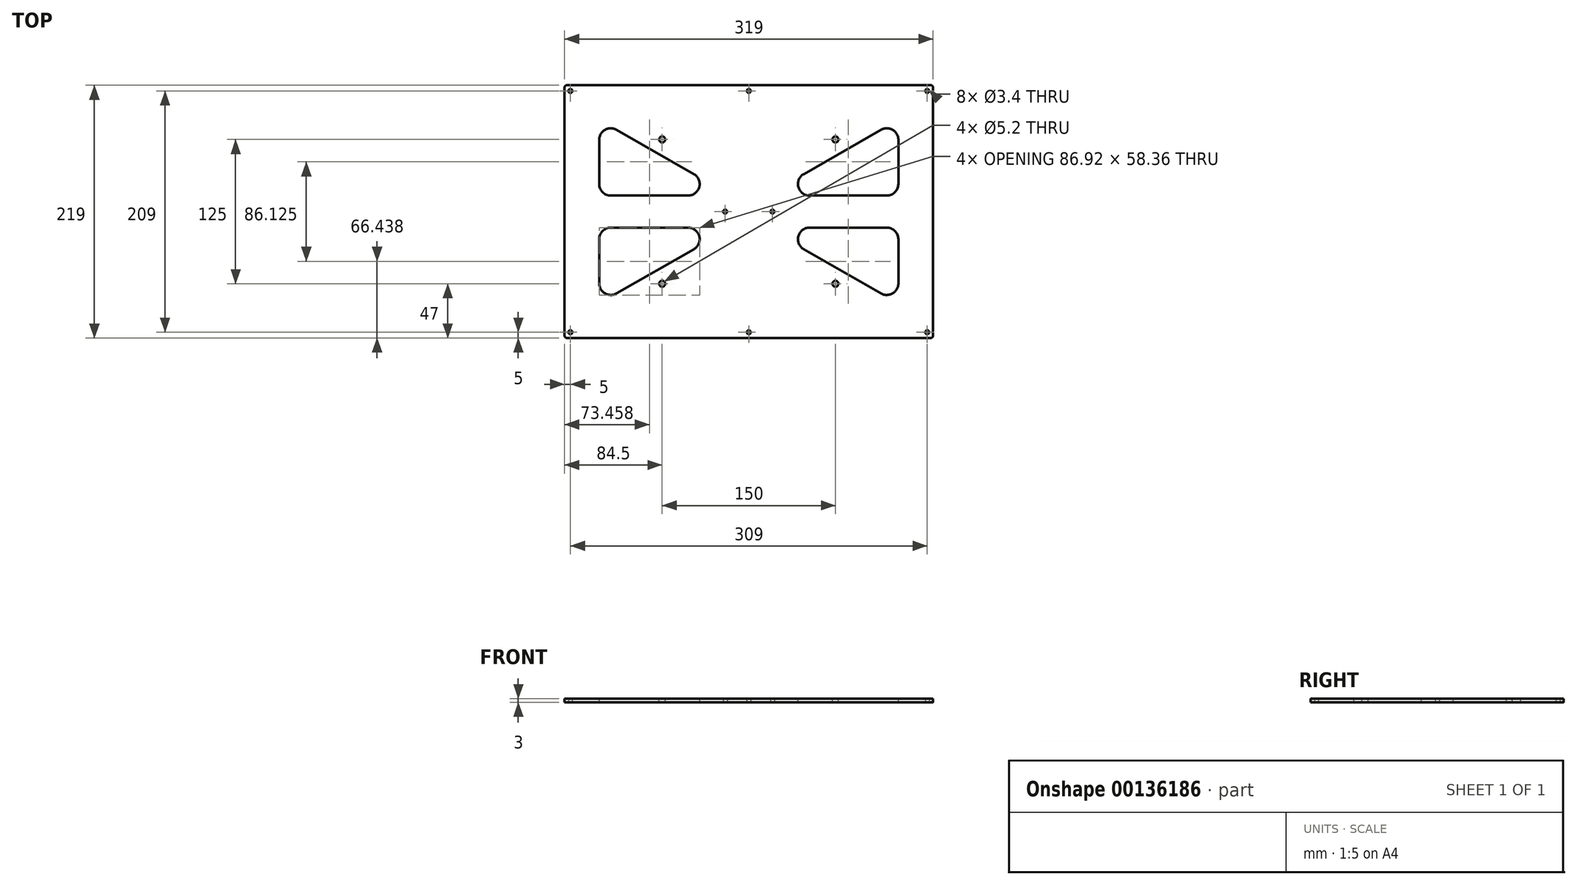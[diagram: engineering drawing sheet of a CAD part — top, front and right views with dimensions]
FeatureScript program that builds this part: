
annotation { "Feature Type Name" : "Feature", "Feature Type Description" : "" }
export const myFeature = defineFeature(function(context is Context, id is Id, definition is map)
    precondition{}
    {
        {
            var Q0;
            Q0=qCreatedBy(makeId("Top.planeOp"),FACE);
            var sketch = newSketch(context, id + "F0", { "sketchPlane" : qUnion([Q0])});
            skLineSegment(sketch, "E0.bottom", {"start": v(157.5, -109.5) * mm, "end": v(-157.5, -109.5) * mm});
            skLineSegment(sketch, "E0.top", {"start": v(157.5, 109.5) * mm, "end": v(-157.5, 109.5) * mm});
            skLineSegment(sketch, "E0.left", {"start": v(159.5, -107.5) * mm, "end": v(159.5, 107.5) * mm});
            skLineSegment(sketch, "E0.right", {"start": v(-159.5, -107.5) * mm, "end": v(-159.5, 107.5) * mm});
            skPoint(sketch, "E0.middle", {"position": v(0, 0) * mm});
            skPoint(sketch, "E1.visualSharp", {"position": v(-159.5, 109.5) * mm});
            skArc(sketch, "E1.filletArc", {"start": v(-157.5, 109.5) * mm, "mid": v(-158.91, 108.91) * mm, "end": v(-159.5, 107.5) * mm});
            skPoint(sketch, "E2.visualSharp", {"position": v(159.5, 109.5) * mm});
            skArc(sketch, "E2.filletArc", {"start": v(159.5, 107.5) * mm, "mid": v(158.91, 108.91) * mm, "end": v(157.5, 109.5) * mm});
            skPoint(sketch, "E3.visualSharp", {"position": v(159.5, -109.5) * mm});
            skArc(sketch, "E3.filletArc", {"start": v(157.5, -109.5) * mm, "mid": v(158.91, -108.91) * mm, "end": v(159.5, -107.5) * mm});
            skPoint(sketch, "E4.visualSharp", {"position": v(-159.5, -109.5) * mm});
            skArc(sketch, "E4.filletArc", {"start": v(-159.5, -107.5) * mm, "mid": v(-158.91, -108.91) * mm, "end": v(-157.5, -109.5) * mm});
            skLineSegment(sketch, "E5.bottom", {"start": v(154.5, -104.5) * mm, "end": v(-154.5, -104.5) * mm, "construction": true});
            skLineSegment(sketch, "E5.top", {"start": v(154.5, 104.5) * mm, "end": v(-154.5, 104.5) * mm, "construction": true});
            skLineSegment(sketch, "E5.left", {"start": v(154.5, -104.5) * mm, "end": v(154.5, 104.5) * mm, "construction": true});
            skLineSegment(sketch, "E5.right", {"start": v(-154.5, -104.5) * mm, "end": v(-154.5, 104.5) * mm, "construction": true});
            skLineSegment(sketch, "E6", {"start": v(0, 104.5) * mm, "end": v(0, -104.5) * mm, "construction": true});
            skCircle(sketch, "E7", {"center": v(-154.5, 104.5) * mm, "radius": 1.7 * mm});
            skCircle(sketch, "E8", {"center": v(0, 104.5) * mm, "radius": 1.7 * mm});
            skCircle(sketch, "E9", {"center": v(154.5, 104.5) * mm, "radius": 1.7 * mm});
            skCircle(sketch, "E10", {"center": v(154.5, -104.5) * mm, "radius": 1.7 * mm});
            skCircle(sketch, "E11", {"center": v(0, -104.5) * mm, "radius": 1.7 * mm});
            skCircle(sketch, "E12", {"center": v(-154.5, -104.5) * mm, "radius": 1.7 * mm});
            skLineSegment(sketch, "E13", {"start": v(-154.5, 0) * mm, "end": v(159.5, 0) * mm, "construction": true});
            skCircle(sketch, "E14", {"center": v(-20.5, 0) * mm, "radius": 1.7 * mm});
            skCircle(sketch, "E15", {"center": v(20.5, 0) * mm, "radius": 1.7 * mm});
            skSolve(sketch);
        }
        {
            var Q0;
            Q0 = qSketchRegion(id + "F0", true);
            extrude(context, id + "F1", {"entities" : qUnion([Q0]), "depth" : 3 * mm});
        }
        {
            var Q0;
            Q0=makeQuery(id+"F1.opExtrude","CAP_FACE",FACE,{"disambiguationData":[OSD([sQuery(id+"F0.wireOp",EDGE,"E0.bottom"),sQuery(id+"F0.wireOp",EDGE,"E0.top"),sQuery(id+"F0.wireOp",EDGE,"E0.left"),sQuery(id+"F0.wireOp",EDGE,"E0.right"),sQuery(id+"F0.wireOp",EDGE,"E1.filletArc"),sQuery(id+"F0.wireOp",EDGE,"E2.filletArc"),sQuery(id+"F0.wireOp",EDGE,"E3.filletArc"),sQuery(id+"F0.wireOp",EDGE,"E4.filletArc"),sQuery(id+"F0.wireOp",EDGE,"E7"),sQuery(id+"F0.wireOp",EDGE,"E8"),sQuery(id+"F0.wireOp",EDGE,"E9"),sQuery(id+"F0.wireOp",EDGE,"E10"),sQuery(id+"F0.wireOp",EDGE,"E11"),sQuery(id+"F0.wireOp",EDGE,"E12"),sQuery(id+"F0.wireOp",EDGE,"E14"),sQuery(id+"F0.wireOp",EDGE,"E15")])],"isStart":false});
            var sketch = newSketch(context, id + "F2", { "sketchPlane" : qUnion([Q0])});
            skLineSegment(sketch, "E16.left", {"start": v(129.5, -62.24) * mm, "end": v(129.5, -23.88) * mm});
            skLineSegment(sketch, "E16.right", {"start": v(-129.5, -62.24) * mm, "end": v(-129.5, -23.88) * mm});
            skPoint(sketch, "E16.middle", {"position": v(0, 0) * mm});
            skLineSegment(sketch, "E17.bottom", {"start": v(119.5, -13.88) * mm, "end": v(52.56, -13.88) * mm});
            skLineSegment(sketch, "E17.top", {"start": v(119.5, 13.88) * mm, "end": v(52.56, 13.88) * mm});
            skLineSegment(sketch, "E18.trimOffspring", {"start": v(129.5, 23.88) * mm, "end": v(129.5, 62.24) * mm});
            skLineSegment(sketch, "E19.trimOffspring", {"start": v(-129.5, 23.88) * mm, "end": v(-129.5, 62.24) * mm});
            skLineSegment(sketch, "E20.trimOffspring", {"start": v(-52.56, 13.88) * mm, "end": v(-119.5, 13.88) * mm});
            skLineSegment(sketch, "E21.trimOffspring", {"start": v(-52.56, -13.88) * mm, "end": v(-119.5, -13.88) * mm});
            skLineSegment(sketch, "E22", {"start": v(-47.59, -32.56) * mm, "end": v(-114.53, -70.92) * mm});
            skLineSegment(sketch, "E23", {"start": v(47.59, -32.56) * mm, "end": v(114.53, -70.92) * mm});
            skLineSegment(sketch, "E24", {"start": v(47.59, 32.56) * mm, "end": v(114.53, 70.92) * mm});
            skLineSegment(sketch, "E25", {"start": v(-47.59, 32.56) * mm, "end": v(-114.53, 70.92) * mm});
            skPoint(sketch, "E26.top.end.orphan", {"position": v(-15, 79.5) * mm});
            skPoint(sketch, "E16.top.end.orphan", {"position": v(15, 79.5) * mm});
            skPoint(sketch, "E27.visualSharp", {"position": v(-129.5, 13.88) * mm});
            skArc(sketch, "E27.filletArc", {"start": v(-129.5, 23.88) * mm, "mid": v(-126.57, 16.81) * mm, "end": v(-119.5, 13.88) * mm});
            skPoint(sketch, "E28.visualSharp", {"position": v(-129.5, 79.5) * mm});
            skArc(sketch, "E28.filletArc", {"start": v(-114.53, 70.92) * mm, "mid": v(-124.51, 70.9) * mm, "end": v(-129.5, 62.24) * mm});
            skPoint(sketch, "E29.visualSharp", {"position": v(-15, 13.88) * mm});
            skArc(sketch, "E29.filletArc", {"start": v(-52.56, 13.88) * mm, "mid": v(-42.9, 21.3) * mm, "end": v(-47.59, 32.56) * mm});
            skPoint(sketch, "E30.visualSharp", {"position": v(-15, -13.88) * mm});
            skArc(sketch, "E30.filletArc", {"start": v(-47.59, -32.56) * mm, "mid": v(-42.9, -21.3) * mm, "end": v(-52.56, -13.88) * mm});
            skPoint(sketch, "E31.visualSharp", {"position": v(-129.5, -13.88) * mm});
            skArc(sketch, "E31.filletArc", {"start": v(-119.5, -13.88) * mm, "mid": v(-126.57, -16.81) * mm, "end": v(-129.5, -23.88) * mm});
            skPoint(sketch, "E32.visualSharp", {"position": v(-129.5, -79.5) * mm});
            skArc(sketch, "E32.filletArc", {"start": v(-129.5, -62.24) * mm, "mid": v(-124.51, -70.9) * mm, "end": v(-114.53, -70.92) * mm});
            skPoint(sketch, "E33.visualSharp", {"position": v(15, -13.88) * mm});
            skArc(sketch, "E33.filletArc", {"start": v(52.56, -13.88) * mm, "mid": v(42.9, -21.3) * mm, "end": v(47.59, -32.56) * mm});
            skPoint(sketch, "E34.visualSharp", {"position": v(129.5, -13.88) * mm});
            skArc(sketch, "E34.filletArc", {"start": v(129.5, -23.88) * mm, "mid": v(126.57, -16.81) * mm, "end": v(119.5, -13.88) * mm});
            skPoint(sketch, "E35.visualSharp", {"position": v(129.5, -79.5) * mm});
            skArc(sketch, "E35.filletArc", {"start": v(114.53, -70.92) * mm, "mid": v(124.51, -70.9) * mm, "end": v(129.5, -62.24) * mm});
            skPoint(sketch, "E36.visualSharp", {"position": v(15, 13.88) * mm});
            skArc(sketch, "E36.filletArc", {"start": v(47.59, 32.56) * mm, "mid": v(42.9, 21.3) * mm, "end": v(52.56, 13.88) * mm});
            skPoint(sketch, "E37.visualSharp", {"position": v(129.5, 79.5) * mm});
            skArc(sketch, "E37.filletArc", {"start": v(129.5, 62.24) * mm, "mid": v(124.51, 70.9) * mm, "end": v(114.53, 70.92) * mm});
            skPoint(sketch, "E38.visualSharp", {"position": v(129.5, 13.88) * mm});
            skArc(sketch, "E38.filletArc", {"start": v(119.5, 13.88) * mm, "mid": v(126.57, 16.81) * mm, "end": v(129.5, 23.88) * mm});
            skSolve(sketch);
        }
        {
            var Q0;
            Q0=makeQuery(id+"F2.imprint","IMPRINT",FACE,{"disambiguationData":[TD([[makeQuery(id+"F2.imprint","IMPRINT",EDGE,{"derivedFrom":sQuery(id+"F2.wireOp",EDGE,"E19.trimOffspring")}),-1.0]])]});
            var Q1;
            Q1=makeQuery(id+"F2.imprint","IMPRINT",FACE,{"disambiguationData":[TD([[makeQuery(id+"F2.imprint","IMPRINT",EDGE,{"derivedFrom":sQuery(id+"F2.wireOp",EDGE,"E17.top")}),-1.0]])]});
            var Q2;
            Q2=makeQuery(id+"F2.imprint","IMPRINT",FACE,{"disambiguationData":[TD([[makeQuery(id+"F2.imprint","IMPRINT",EDGE,{"derivedFrom":sQuery(id+"F2.wireOp",EDGE,"E16.left")}),1.0]])]});
            var Q3;
            Q3=makeQuery(id+"F2.imprint","IMPRINT",FACE,{"disambiguationData":[TD([[makeQuery(id+"F2.imprint","IMPRINT",EDGE,{"derivedFrom":sQuery(id+"F2.wireOp",EDGE,"E16.right")}),-1.0]])]});
            extrude(context, id + "F3", {"entities" : qUnion([Q0, Q1, Q2, Q3]), "operationType" : NewBodyOperationType.REMOVE, "endBound" : BoundingType.THROUGH_ALL, "oppositeDirection" : true, "depth" : 25 * mm});
        }
        {
            var Q0;
            Q0=makeQuery(id+"F1.opExtrude","CAP_FACE",FACE,{"disambiguationData":[OSD([sQuery(id+"F0.wireOp",EDGE,"E0.bottom"),sQuery(id+"F0.wireOp",EDGE,"E0.top"),sQuery(id+"F0.wireOp",EDGE,"E0.left"),sQuery(id+"F0.wireOp",EDGE,"E0.right"),sQuery(id+"F0.wireOp",EDGE,"E1.filletArc"),sQuery(id+"F0.wireOp",EDGE,"E2.filletArc"),sQuery(id+"F0.wireOp",EDGE,"E3.filletArc"),sQuery(id+"F0.wireOp",EDGE,"E4.filletArc"),sQuery(id+"F0.wireOp",EDGE,"E7"),sQuery(id+"F0.wireOp",EDGE,"E8"),sQuery(id+"F0.wireOp",EDGE,"E9"),sQuery(id+"F0.wireOp",EDGE,"E10"),sQuery(id+"F0.wireOp",EDGE,"E11"),sQuery(id+"F0.wireOp",EDGE,"E12"),sQuery(id+"F0.wireOp",EDGE,"E14"),sQuery(id+"F0.wireOp",EDGE,"E15")])],"isStart":false});
            var sketch = newSketch(context, id + "F4", { "sketchPlane" : qUnion([Q0])});
            skLineSegment(sketch, "E39.bottom", {"start": v(75, -62.5) * mm, "end": v(-75, -62.5) * mm, "construction": true});
            skLineSegment(sketch, "E39.top", {"start": v(75, 62.5) * mm, "end": v(-75, 62.5) * mm, "construction": true});
            skLineSegment(sketch, "E39.left", {"start": v(75, -62.5) * mm, "end": v(75, 62.5) * mm, "construction": true});
            skLineSegment(sketch, "E39.right", {"start": v(-75, -62.5) * mm, "end": v(-75, 62.5) * mm, "construction": true});
            skPoint(sketch, "E39.middle", {"position": v(0, 0) * mm});
            skCircle(sketch, "E40", {"center": v(-75, 62.5) * mm, "radius": 2.6 * mm});
            skCircle(sketch, "E41.0.1.0", {"center": v(-75, -62.5) * mm, "radius": 2.6 * mm});
            skCircle(sketch, "E41.1.0.0", {"center": v(75, 62.5) * mm, "radius": 2.6 * mm});
            skCircle(sketch, "E41.1.1.0", {"center": v(75, -62.5) * mm, "radius": 2.6 * mm});
            skLineSegment(sketch, "E41.direction1", {"start": v(-75, 62.5) * mm, "end": v(75, 62.5) * mm, "construction": true});
            skLineSegment(sketch, "E41.direction2", {"start": v(-75, 62.5) * mm, "end": v(-75, -62.5) * mm, "construction": true});
            skSolve(sketch);
        }
        {
            var Q0;
            Q0 = qSketchRegion(id + "F4", true);
            extrude(context, id + "F5", {"entities" : qUnion([Q0]), "operationType" : NewBodyOperationType.REMOVE, "oppositeDirection" : true, "depth" : 25 * mm});
        }
    });
